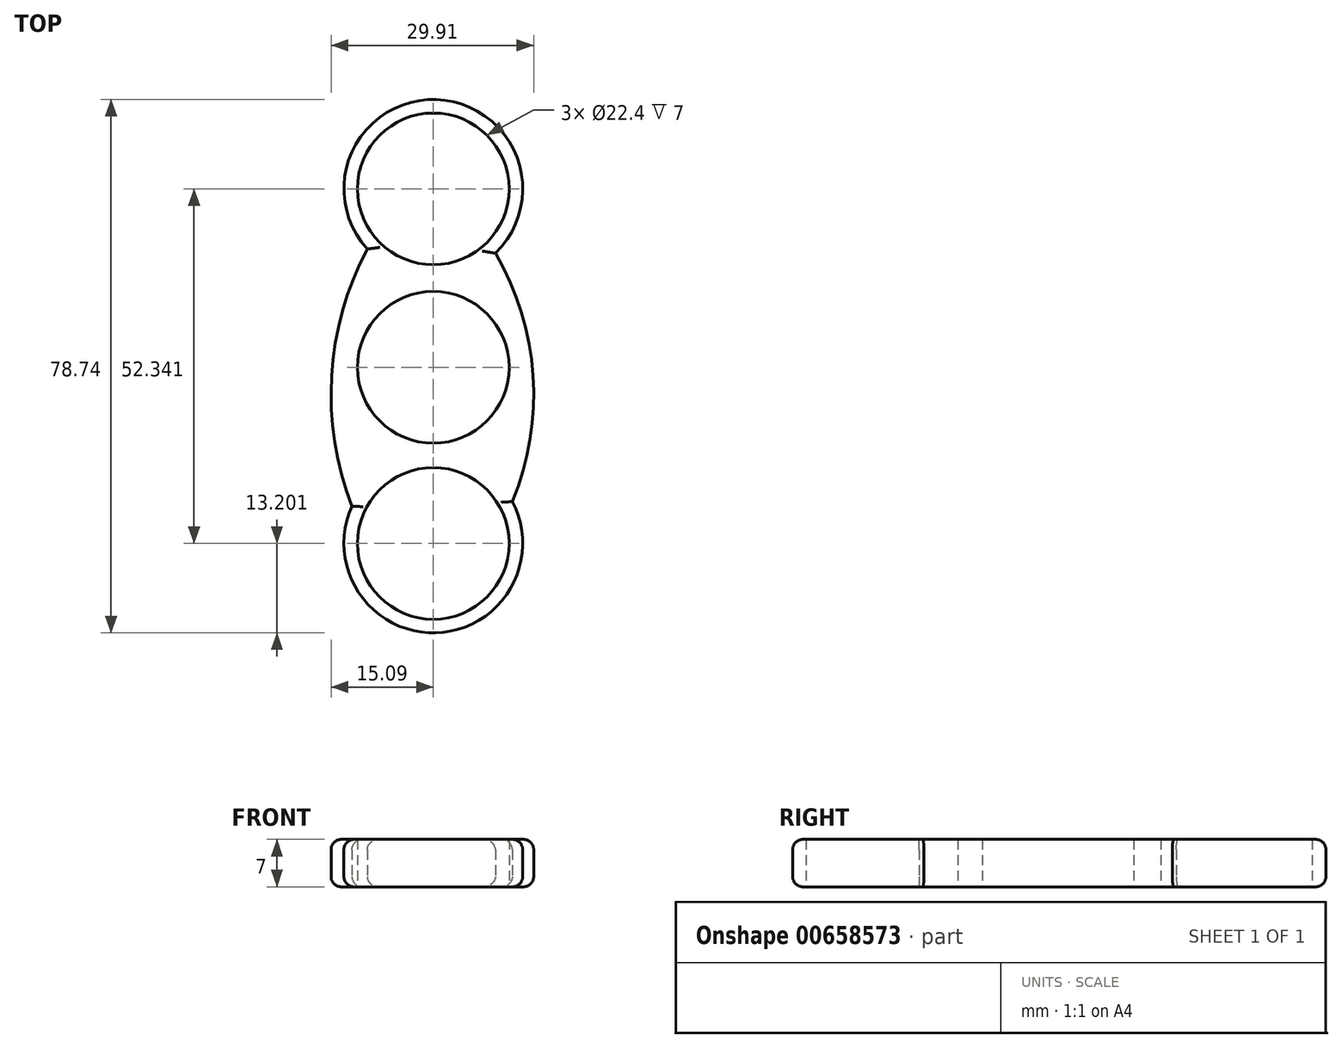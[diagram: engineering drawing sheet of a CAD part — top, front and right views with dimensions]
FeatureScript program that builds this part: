
annotation { "Feature Type Name" : "Feature", "Feature Type Description" : "" }
export const myFeature = defineFeature(function(context is Context, id is Id, definition is map)
    precondition{}
    {
        {
            var Q0;
            Q0=qCreatedBy(makeId("Top.planeOp"),FACE);
            var sketch = newSketch(context, id + "F0", { "sketchPlane" : qUnion([Q0])});
            skCircle(sketch, "E0", {"center": v(0, 0) * mm, "radius": 11.2 * mm});
            skCircle(sketch, "E1", {"center": v(0, 26.34) * mm, "radius": 11.2 * mm});
            skCircle(sketch, "E2", {"center": v(0, -26) * mm, "radius": 11.2 * mm});
            skArc(sketch, "E3", {"start": v(-12, -20.52) * mm, "mid": v(0.38, -39.2) * mm, "end": v(11.67, -19.83) * mm});
            skArc(sketch, "E4", {"start": v(-9.76, 17.46) * mm, "mid": v(-15.01, -1.28) * mm, "end": v(-12, -20.52) * mm});
            skArc(sketch, "E5", {"start": v(11.67, -19.83) * mm, "mid": v(14.73, -1.2) * mm, "end": v(9.18, 16.86) * mm});
            skArc(sketch, "E6.trimOffspring", {"start": v(9.18, 16.86) * mm, "mid": v(0.42, 39.54) * mm, "end": v(-9.76, 17.46) * mm});
            skSolve(sketch);
        }
        {
            var Q0;
            Q0 = qSketchRegion(id + "F0", true);
            extrude(context, id + "F1", {"entities" : qUnion([Q0]), "depth" : 7 * mm, "offsetDistance" : 25 * mm});
        }
        {
            var Q0;
            Q0=makeQuery(id+"F1.opExtrude","CAP_EDGE",EDGE,{"disambiguationData":[OSD([sQuery(id+"F0.wireOp",EDGE,"E3")])],"isStart":false});
            var Q1;
            Q1=makeQuery(id+"F1.opExtrude","CAP_EDGE",EDGE,{"disambiguationData":[OSD([sQuery(id+"F0.wireOp",EDGE,"E3")])],"isStart":true});
            var Q2;
            Q2=makeQuery(id+"F1.opExtrude","CAP_EDGE",EDGE,{"disambiguationData":[OSD([sQuery(id+"F0.wireOp",EDGE,"E5")])],"isStart":false});
            var Q3;
            Q3=makeQuery(id+"F1.opExtrude","CAP_EDGE",EDGE,{"disambiguationData":[OSD([sQuery(id+"F0.wireOp",EDGE,"E5")])],"isStart":true});
            var Q4;
            Q4=makeQuery(id+"F1.opExtrude","CAP_EDGE",EDGE,{"disambiguationData":[OSD([sQuery(id+"F0.wireOp",EDGE,"E6.trimOffspring")])],"isStart":false});
            var Q5;
            Q5=makeQuery(id+"F1.opExtrude","CAP_EDGE",EDGE,{"disambiguationData":[OSD([sQuery(id+"F0.wireOp",EDGE,"E6.trimOffspring")])],"isStart":true});
            var Q6;
            Q6=makeQuery(id+"F1.opExtrude","CAP_EDGE",EDGE,{"disambiguationData":[OSD([sQuery(id+"F0.wireOp",EDGE,"E4")])],"isStart":false});
            var Q7;
            Q7=makeQuery(id+"F1.opExtrude","CAP_EDGE",EDGE,{"disambiguationData":[OSD([sQuery(id+"F0.wireOp",EDGE,"E4")])],"isStart":true});
            fillet(context, id + "F2", {"entities" : qUnion([Q0, Q1, Q2, Q3, Q4, Q5, Q6, Q7]), "radius" : 1.5 * mm, "tangentPropagation" : true, "allowEdgeOverflow" : false});
        }
    });
